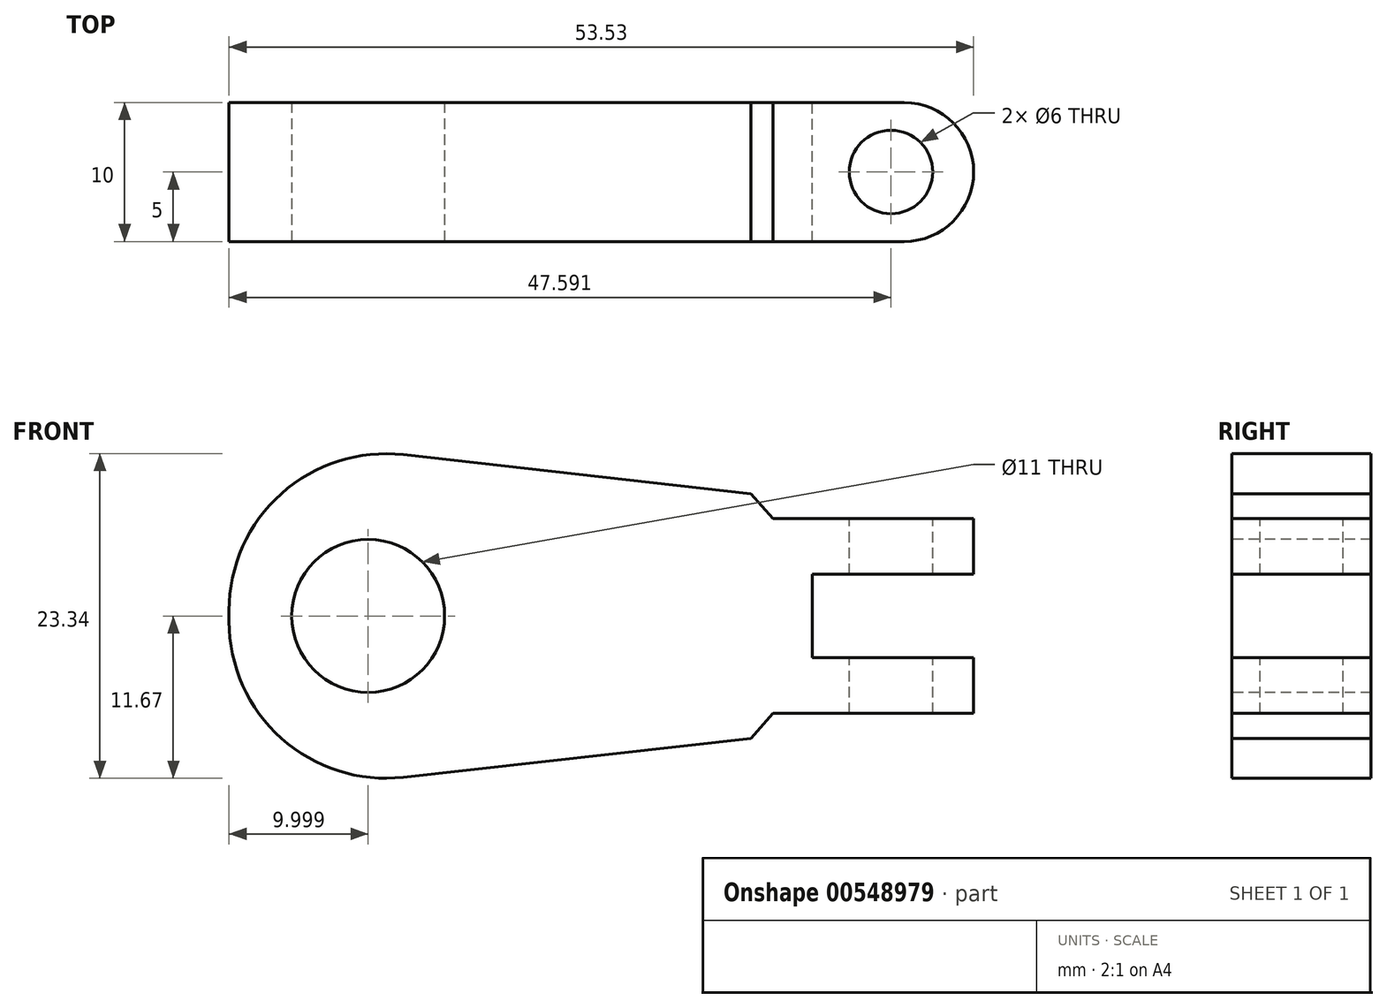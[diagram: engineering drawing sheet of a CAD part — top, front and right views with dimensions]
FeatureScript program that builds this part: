
annotation { "Feature Type Name" : "Feature", "Feature Type Description" : "" }
export const myFeature = defineFeature(function(context is Context, id is Id, definition is map)
    precondition{}
    {
        {
            var Q0;
            Q0=qCreatedBy(makeId("Front.planeOp"),FACE);
            var sketch = newSketch(context, id + "F0", { "sketchPlane" : qUnion([Q0])});
            skLineSegment(sketch, "E0", {"start": v(-29.87, 0) * mm, "end": v(-29.87, 13) * mm});
            skLineSegment(sketch, "E1", {"start": v(23.66, 0) * mm, "end": v(23.66, 7) * mm});
            skLineSegment(sketch, "E2", {"start": v(23.66, 7) * mm, "end": v(-29.87, 13) * mm});
            skLineSegment(sketch, "E3.MirrorCS", {"start": v(23.66, -7) * mm, "end": v(-29.87, -13) * mm});
            skLineSegment(sketch, "E4.MirrorCS", {"start": v(23.66, 0) * mm, "end": v(23.66, -7) * mm});
            skLineSegment(sketch, "E5.MirrorCS", {"start": v(-29.87, 0) * mm, "end": v(-29.87, -13) * mm});
            skSolve(sketch);
        }
        {
            var Q0;
            Q0 = qSketchRegion(id + "F0", true);
            extrude(context, id + "F1", {"entities" : qUnion([Q0]), "depth" : 10 * mm, "offsetDistance" : 25 * mm});
        }
        {
            var Q0;
            Q0=makeQuery(id+"F1.opExtrude","CAP_FACE",FACE,{"disambiguationData":[OSD([sQuery(id+"F0.wireOp",EDGE,"E0"),sQuery(id+"F0.wireOp",EDGE,"E1"),sQuery(id+"F0.wireOp",EDGE,"E2"),sQuery(id+"F0.wireOp",EDGE,"E3.MirrorCS"),sQuery(id+"F0.wireOp",EDGE,"E4.MirrorCS"),sQuery(id+"F0.wireOp",EDGE,"E5.MirrorCS")])],"isStart":false});
            var sketch = newSketch(context, id + "F2", { "sketchPlane" : qUnion([Q0])});
            skLineSegment(sketch, "E6", {"start": v(-29.87, 0) * mm, "end": v(-19.87, 0) * mm});
            skCircle(sketch, "E7", {"center": v(-19.87, 0) * mm, "radius": 5.5 * mm});
            skSolve(sketch);
        }
        {
            var Q0;
            Q0 = qSketchRegion(id + "F2", true);
            extrude(context, id + "F3", {"entities" : qUnion([Q0]), "operationType" : NewBodyOperationType.REMOVE, "oppositeDirection" : true, "depth" : 25 * mm, "offsetDistance" : 25 * mm});
        }
        {
            var Q0;
            Q0=qCreatedBy(makeId("Top.planeOp"),FACE);
            var sketch = newSketch(context, id + "F4", { "sketchPlane" : qUnion([Q0])});
            skLineSegment(sketch, "E8", {"start": v(23.72, 0) * mm, "end": v(23.72, -5) * mm});
            skLineSegment(sketch, "E9", {"start": v(23.72, -5) * mm, "end": v(17.72, -5) * mm});
            skCircle(sketch, "E10", {"center": v(17.72, -5) * mm, "radius": 3 * mm});
            skSolve(sketch);
        }
        {
            var Q0;
            Q0 = qSketchRegion(id + "F4", true);
            extrude(context, id + "F5", {"entities" : qUnion([Q0]), "operationType" : NewBodyOperationType.REMOVE, "endBound" : BoundingType.SYMMETRIC, "oppositeDirection" : true, "depth" : 25 * mm, "offsetDistance" : 25 * mm});
        }
        {
            var Q0;
            Q0=makeQuery(id+"F1.opExtrude","CAP_EDGE",EDGE,{"disambiguationData":[OSD([sQuery(id+"F0.wireOp",EDGE,"E1"),sQuery(id+"F0.wireOp",EDGE,"E4.MirrorCS")])],"isStart":false});
            var Q1;
            Q1=makeQuery(id+"F1.opExtrude","CAP_EDGE",EDGE,{"disambiguationData":[OSD([sQuery(id+"F0.wireOp",EDGE,"E1"),sQuery(id+"F0.wireOp",EDGE,"E4.MirrorCS")])],"isStart":true});
            fillet(context, id + "F6", {"entities" : qUnion([Q0, Q1]), "radius" : 5 * mm, "tangentPropagation" : true, "allowEdgeOverflow" : false});
        }
        {
            var Q0;
            Q0=makeQuery(id+"F1.opExtrude","SWEPT_EDGE",EDGE,{"disambiguationData":[OSD([sQuery(id+"F0.wireOp",EDGE,"E0"),sQuery(id+"F0.wireOp",EDGE,"E2")])]});
            var Q1;
            Q1=makeQuery(id+"F1.opExtrude","SWEPT_EDGE",EDGE,{"disambiguationData":[OSD([sQuery(id+"F0.wireOp",EDGE,"E3.MirrorCS"),sQuery(id+"F0.wireOp",EDGE,"E5.MirrorCS")])]});
            fillet(context, id + "F7", {"entities" : qUnion([Q0, Q1]), "radius" : 11.28 * mm, "tangentPropagation" : true, "allowEdgeOverflow" : false});
        }
        {
            var Q0;
            Q0=qCreatedBy(makeId("Front.planeOp"),FACE);
            var sketch = newSketch(context, id + "F8", { "sketchPlane" : qUnion([Q0])});
            skLineSegment(sketch, "E11", {"start": v(0, 0) * mm, "end": v(24.14, 0) * mm});
            skLineSegment(sketch, "E12", {"start": v(24.14, 0) * mm, "end": v(24.14, -3) * mm});
            skLineSegment(sketch, "E13", {"start": v(24.14, -3) * mm, "end": v(12.08, -3) * mm});
            skLineSegment(sketch, "E14", {"start": v(12.08, -3) * mm, "end": v(12.08, 3) * mm});
            skLineSegment(sketch, "E15", {"start": v(12.08, 3) * mm, "end": v(24.2, 3) * mm});
            skLineSegment(sketch, "E16", {"start": v(24.2, 3) * mm, "end": v(24.14, 0) * mm});
            skLineSegment(sketch, "E17.0", {"start": v(24.14, -7) * mm, "end": v(12.08, -7) * mm});
            skLineSegment(sketch, "E18.0", {"start": v(12.08, 7) * mm, "end": v(24.2, 7) * mm});
            skLineSegment(sketch, "E19", {"start": v(12.08, 7) * mm, "end": v(12.08, 14.72) * mm});
            skLineSegment(sketch, "E20", {"start": v(12.08, 14.72) * mm, "end": v(23.4, 15.35) * mm});
            skLineSegment(sketch, "E21", {"start": v(23.4, 15.35) * mm, "end": v(24.2, 7) * mm});
            skLineSegment(sketch, "E22", {"start": v(12.08, -7) * mm, "end": v(12.08, -17.61) * mm});
            skLineSegment(sketch, "E23", {"start": v(12.08, -17.61) * mm, "end": v(25.23, -17.61) * mm});
            skLineSegment(sketch, "E24", {"start": v(25.23, -17.61) * mm, "end": v(24.14, -7) * mm});
            skSolve(sketch);
        }
        {
            var Q0;
            Q0 = qSketchRegion(id + "F8", true);
            extrude(context, id + "F9", {"entities" : qUnion([Q0]), "operationType" : NewBodyOperationType.REMOVE, "depth" : 25 * mm, "offsetDistance" : 25 * mm});
        }
        {
            var Q0;
            Q0=makeQuery(id+"F9.boolean.opBoolean","INTERSECT",EDGE,{"derivedFrom":[makeQuery(id+"F1.opExtrude","SWEPT_FACE",FACE,{"disambiguationData":[OSD([sQuery(id+"F0.wireOp",EDGE,"E3.MirrorCS")])]}),makeQuery(id+"F9.opExtrude","SWEPT_FACE",FACE,{"disambiguationData":[OSD([sQuery(id+"F8.wireOp",EDGE,"E22")])]})]});
            var Q1;
            Q1=makeQuery(id+"F9.boolean.opBoolean","INTERSECT",EDGE,{"derivedFrom":[makeQuery(id+"F1.opExtrude","SWEPT_FACE",FACE,{"disambiguationData":[OSD([sQuery(id+"F0.wireOp",EDGE,"E2")])]}),makeQuery(id+"F9.opExtrude","SWEPT_FACE",FACE,{"disambiguationData":[OSD([sQuery(id+"F8.wireOp",EDGE,"E19")])]})]});
            chamfer(context, id + "F10", {"entities" : qUnion([Q0, Q1]), "width" : 5 * mm, "tangentPropagation" : true});
        }
    });
